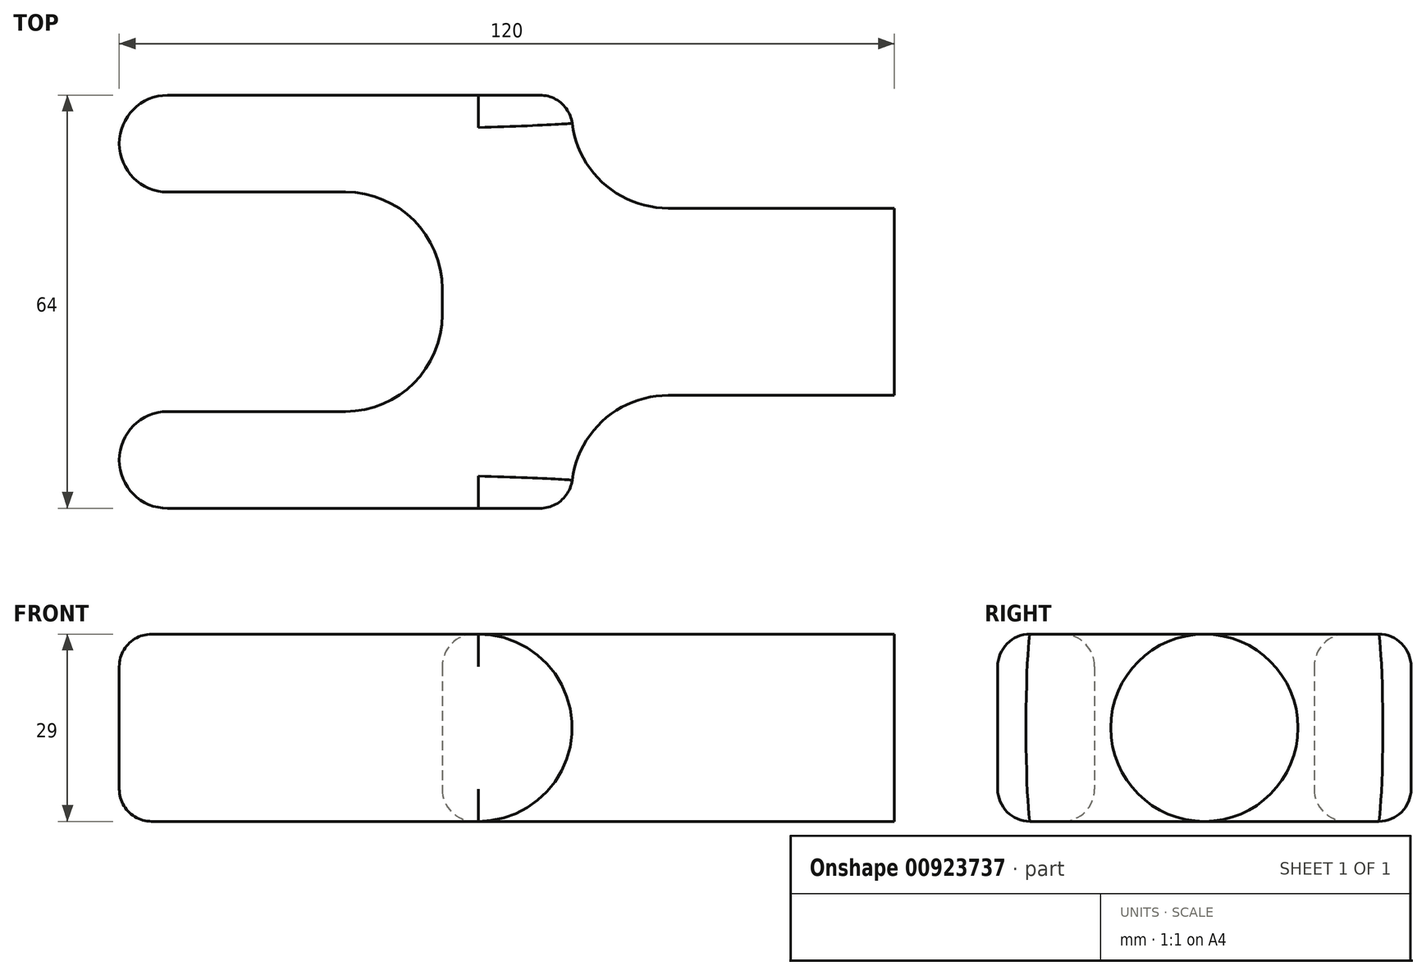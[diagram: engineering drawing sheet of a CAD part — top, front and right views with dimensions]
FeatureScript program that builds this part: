
annotation { "Feature Type Name" : "Feature", "Feature Type Description" : "" }
export const myFeature = defineFeature(function(context is Context, id is Id, definition is map)
    precondition{}
    {
        {
            var Q0;
            Q0=qCreatedBy(makeId("Top.planeOp"),FACE);
            var sketch = newSketch(context, id + "F0", { "sketchPlane" : qUnion([Q0])});
            skLineSegment(sketch, "E0.bottom", {"start": v(0, 0) * mm, "end": v(-35, 0) * mm});
            skLineSegment(sketch, "E0.top", {"start": v(0, -29) * mm, "end": v(-35, -29) * mm});
            skLineSegment(sketch, "E0.left", {"start": v(0, 0) * mm, "end": v(0, -29) * mm});
            skLineSegment(sketch, "E1.bottom", {"start": v(-52, -46.5) * mm, "end": v(-112.5, -46.5) * mm});
            skLineSegment(sketch, "E1.top", {"start": v(-52, 17.5) * mm, "end": v(-112.5, 17.5) * mm});
            skLineSegment(sketch, "E1.left", {"start": v(-50, -44.5) * mm, "end": v(-50, -44) * mm});
            skLineSegment(sketch, "E1.right", {"start": v(-120, -39) * mm, "end": v(-120, -39) * mm});
            skLineSegment(sketch, "E2.bottom", {"start": v(-112.5, -31.5) * mm, "end": v(-85, -31.5) * mm});
            skLineSegment(sketch, "E2.top", {"start": v(-112.5, 2.5) * mm, "end": v(-85, 2.5) * mm});
            skLineSegment(sketch, "E2.right", {"start": v(-70, -16.5) * mm, "end": v(-70, -12.5) * mm});
            skLineSegment(sketch, "E3.trimOffspring", {"start": v(-120, 10) * mm, "end": v(-120, 10) * mm});
            skPoint(sketch, "E4.visualSharp", {"position": v(-120, -46.5) * mm});
            skArc(sketch, "E4.filletArc", {"start": v(-120, -39) * mm, "mid": v(-117.8, -44.3) * mm, "end": v(-112.5, -46.5) * mm});
            skPoint(sketch, "E5.visualSharp", {"position": v(-120, -31.5) * mm});
            skArc(sketch, "E5.filletArc", {"start": v(-112.5, -31.5) * mm, "mid": v(-117.8, -33.7) * mm, "end": v(-120, -39) * mm});
            skPoint(sketch, "E6.visualSharp", {"position": v(-70, -31.5) * mm});
            skArc(sketch, "E6.filletArc", {"start": v(-85, -31.5) * mm, "mid": v(-74.4, -27.1) * mm, "end": v(-70, -16.5) * mm});
            skPoint(sketch, "E7.visualSharp", {"position": v(-70, 2.5) * mm});
            skArc(sketch, "E7.filletArc", {"start": v(-70, -12.5) * mm, "mid": v(-74.4, -1.9) * mm, "end": v(-85, 2.5) * mm});
            skPoint(sketch, "E8.visualSharp", {"position": v(-120, 2.5) * mm});
            skArc(sketch, "E8.filletArc", {"start": v(-120, 10) * mm, "mid": v(-117.8, 4.7) * mm, "end": v(-112.5, 2.5) * mm});
            skPoint(sketch, "E9.visualSharp", {"position": v(-120, 17.5) * mm});
            skArc(sketch, "E9.filletArc", {"start": v(-112.5, 17.5) * mm, "mid": v(-117.8, 15.3) * mm, "end": v(-120, 10) * mm});
            skPoint(sketch, "E10.visualSharp", {"position": v(-50, -46.5) * mm});
            skArc(sketch, "E10.filletArc", {"start": v(-52, -46.5) * mm, "mid": v(-50.59, -45.91) * mm, "end": v(-50, -44.5) * mm});
            skPoint(sketch, "E11.visualSharp", {"position": v(-50, 17.5) * mm});
            skArc(sketch, "E11.filletArc", {"start": v(-50, 15.5) * mm, "mid": v(-50.59, 16.91) * mm, "end": v(-52, 17.5) * mm});
            skLineSegment(sketch, "E12.trimOffspring", {"start": v(-50, 15) * mm, "end": v(-50, 15.5) * mm});
            skPoint(sketch, "E13.visualSharp", {"position": v(-50, -29) * mm});
            skArc(sketch, "E13.filletArc", {"start": v(-35, -29) * mm, "mid": v(-45.6, -33.4) * mm, "end": v(-50, -44) * mm});
            skPoint(sketch, "E14.visualSharp", {"position": v(-50, 0) * mm});
            skArc(sketch, "E14.filletArc", {"start": v(-50, 15) * mm, "mid": v(-45.6, 4.4) * mm, "end": v(-35, 0) * mm});
            skSolve(sketch);
        }
        {
            var Q0;
            Q0 = qSketchRegion(id + "F0", true);
            extrude(context, id + "F1", {"entities" : qUnion([Q0]), "depth" : 14.5 * mm, "offsetDistance" : 25 * mm, "hasSecondDirection" : true, "secondDirectionOppositeDirection" : true, "secondDirectionDepth" : 14.5 * mm});
        }
        {
            var Q0;
            Q0=makeQuery(id+"F1.opExtrude","CAP_EDGE",EDGE,{"disambiguationData":[OSD([sQuery(id+"F0.wireOp",EDGE,"E0.top")])],"isStart":false});
            var Q1;
            Q1=makeQuery(id+"F1.opExtrude","CAP_EDGE",EDGE,{"disambiguationData":[OSD([sQuery(id+"F0.wireOp",EDGE,"E0.bottom")])],"isStart":false});
            var Q2;
            Q2=makeQuery(id+"F1.opExtrude","CAP_EDGE",EDGE,{"disambiguationData":[OSD([sQuery(id+"F0.wireOp",EDGE,"E0.top")])],"isStart":true});
            var Q3;
            Q3=makeQuery(id+"F1.opExtrude","CAP_EDGE",EDGE,{"disambiguationData":[OSD([sQuery(id+"F0.wireOp",EDGE,"E0.bottom")])],"isStart":true});
            var Q4;
            Q4=makeQuery(id+"F1.opExtrude","CAP_EDGE",EDGE,{"disambiguationData":[OSD([sQuery(id+"F0.wireOp",EDGE,"E14.filletArc")])],"isStart":true});
            var Q5;
            Q5=makeQuery(id+"F1.opExtrude","CAP_EDGE",EDGE,{"disambiguationData":[OSD([sQuery(id+"F0.wireOp",EDGE,"E13.filletArc")])],"isStart":true});
            var Q6;
            Q6=makeQuery(id+"F1.opExtrude","CAP_EDGE",EDGE,{"disambiguationData":[OSD([sQuery(id+"F0.wireOp",EDGE,"E14.filletArc")])],"isStart":false});
            var Q7;
            Q7=makeQuery(id+"F1.opExtrude","CAP_EDGE",EDGE,{"disambiguationData":[OSD([sQuery(id+"F0.wireOp",EDGE,"E13.filletArc")])],"isStart":false});
            fillet(context, id + "F2", {"entities" : qUnion([Q0, Q1, Q2, Q3, Q4, Q5, Q6, Q7]), "radius" : 14.5 * mm, "allowEdgeOverflow" : false});
        }
        {
            var Q0;
            Q0=makeQuery(id+"F1.opExtrude","CAP_EDGE",EDGE,{"disambiguationData":[OSD([sQuery(id+"F0.wireOp",EDGE,"E1.top")])],"isStart":true});
            var Q1;
            Q1=makeQuery(id+"F2.opFillet","BLEND_EDGE",EDGE,{"blendedFrom":[makeQuery(id+"F1.opExtrude","CAP_EDGE",EDGE,{"disambiguationData":[OSD([sQuery(id+"F0.wireOp",EDGE,"E14.filletArc")])],"isStart":true}),makeQuery(id+"F1.opExtrude","SWEPT_FACE",FACE,{"disambiguationData":[OSD([sQuery(id+"F0.wireOp",EDGE,"E1.top")])]})],"blendedInto":[makeQuery(id+"F1.opExtrude","SWEPT_FACE",FACE,{"disambiguationData":[OSD([sQuery(id+"F0.wireOp",EDGE,"E1.top")])]})]});
            var Q2;
            Q2=makeQuery(id+"F1.opExtrude","CAP_EDGE",EDGE,{"disambiguationData":[OSD([sQuery(id+"F0.wireOp",EDGE,"E1.top")])],"isStart":false});
            fillet(context, id + "F3", {"entities" : qUnion([Q0, Q1, Q2]), "radius" : 5 * mm, "tangentPropagation" : true, "allowEdgeOverflow" : false});
        }
    });
